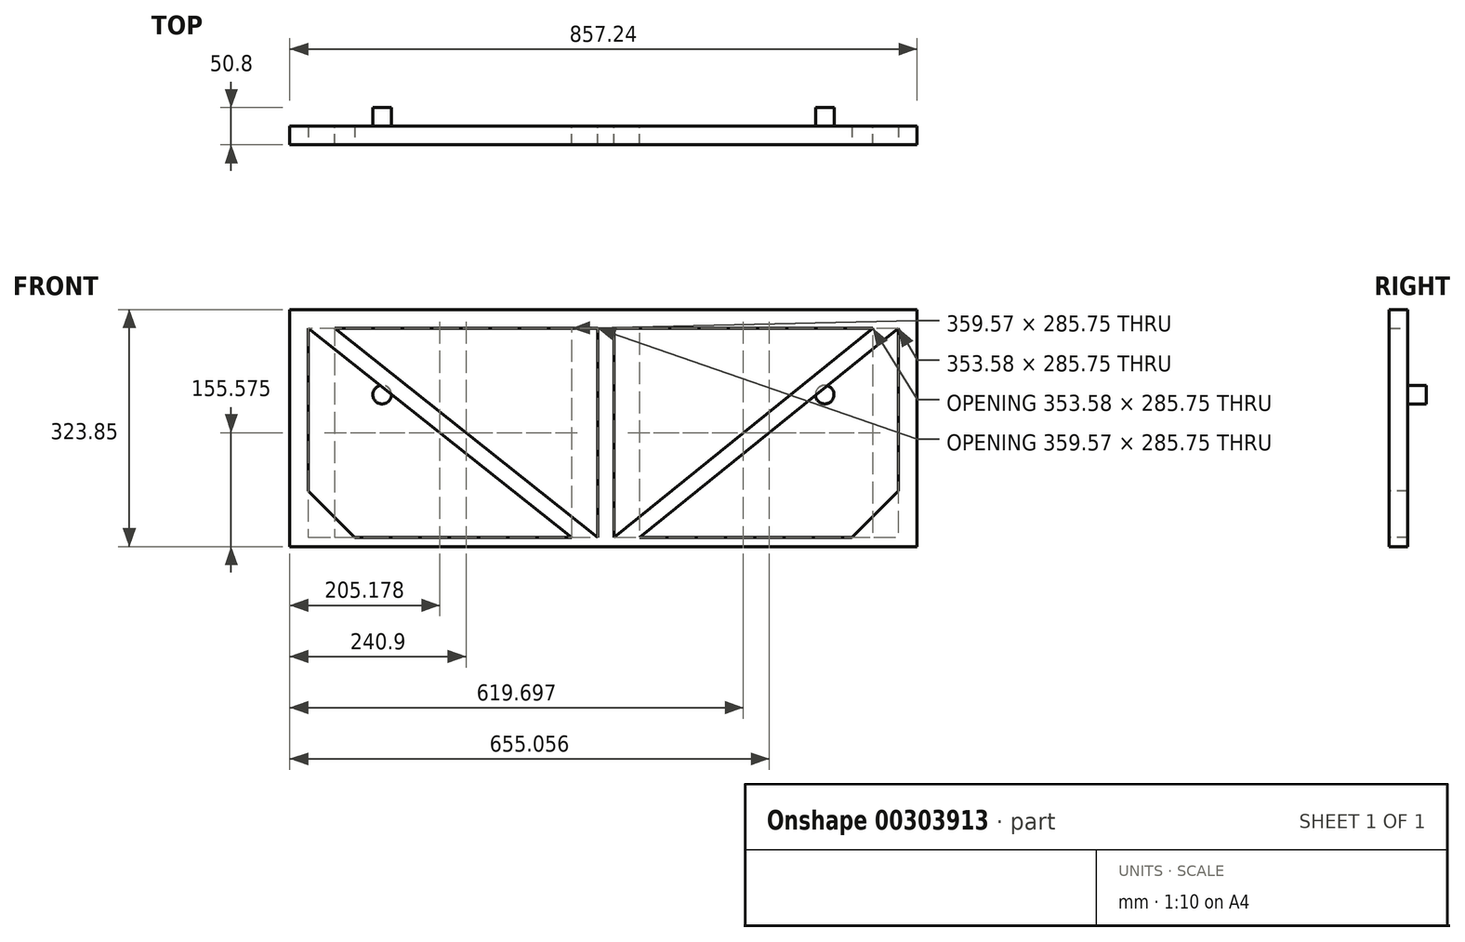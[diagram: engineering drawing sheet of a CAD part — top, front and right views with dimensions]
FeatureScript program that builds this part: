
annotation { "Feature Type Name" : "Feature", "Feature Type Description" : "" }
export const myFeature = defineFeature(function(context is Context, id is Id, definition is map)
    precondition{}
    {
        {
            var Q0;
            Q0=qCreatedBy(makeId("Front.planeOp"),FACE);
            var sketch = newSketch(context, id + "F0", { "sketchPlane" : qUnion([Q0])});
            skLineSegment(sketch, "E0.bottom", {"start": v(-428.63, 0) * mm, "end": v(428.63, 0) * mm, "construction": true});
            skLineSegment(sketch, "E0.left", {"start": v(-428.63, 0) * mm, "end": v(-428.63, 12.7) * mm, "construction": true});
            skLineSegment(sketch, "E0.right", {"start": v(428.63, 0) * mm, "end": v(428.63, 12.7) * mm, "construction": true});
            skLineSegment(sketch, "E1.left", {"start": v(428.63, 12.7) * mm, "end": v(428.63, 298.45) * mm});
            skLineSegment(sketch, "E1.right", {"start": v(403.23, 12.7) * mm, "end": v(403.23, 298.45) * mm});
            skLineSegment(sketch, "E2", {"start": v(-7.94, 12.7) * mm, "end": v(-7.94, 298.45) * mm});
            skLineSegment(sketch, "E3", {"start": v(14.29, 298.45) * mm, "end": v(14.29, 12.7) * mm});
            skLineSegment(sketch, "E4.top", {"start": v(-428.62, 323.85) * mm, "end": v(428.62, 323.85) * mm});
            skLineSegment(sketch, "E4.left", {"start": v(-428.62, 298.45) * mm, "end": v(-428.62, 323.85) * mm});
            skLineSegment(sketch, "E4.right", {"start": v(428.63, 298.45) * mm, "end": v(428.63, 323.85) * mm});
            skLineSegment(sketch, "E5.left", {"start": v(-428.63, 298.45) * mm, "end": v(-428.63, 12.7) * mm});
            skLineSegment(sketch, "E5.right", {"start": v(-403.23, 298.45) * mm, "end": v(-403.23, 12.7) * mm});
            skLineSegment(sketch, "E6", {"start": v(-403.23, 298.45) * mm, "end": v(-43.66, 12.7) * mm});
            skLineSegment(sketch, "E7", {"start": v(-7.94, 12.7) * mm, "end": v(-367.5, 298.45) * mm});
            skLineSegment(sketch, "E8", {"start": v(14.29, 12.7) * mm, "end": v(367.87, 298.45) * mm});
            skLineSegment(sketch, "E9", {"start": v(403.23, 298.45) * mm, "end": v(49.65, 12.7) * mm});
            skLineSegment(sketch, "E10.trimOffspring", {"start": v(-367.5, 298.45) * mm, "end": v(-7.94, 298.45) * mm});
            skLineSegment(sketch, "E11.trimOffspring", {"start": v(14.29, 298.45) * mm, "end": v(367.87, 298.45) * mm});
            skLineSegment(sketch, "E12.trimOffspring", {"start": v(403.23, 12.7) * mm, "end": v(428.63, 12.7) * mm});
            skLineSegment(sketch, "E13", {"start": v(-428.63, 12.7) * mm, "end": v(-403.23, 12.7) * mm});
            skLineSegment(sketch, "E14.trimOffspring", {"start": v(-43.66, 12.7) * mm, "end": v(49.65, 12.7) * mm});
            skLineSegment(sketch, "E15.bottom", {"start": v(-428.63, 12.7) * mm, "end": v(428.63, 12.7) * mm});
            skLineSegment(sketch, "E15.top", {"start": v(-428.63, 0) * mm, "end": v(428.63, 0) * mm});
            skLineSegment(sketch, "E15.left", {"start": v(-428.63, 12.7) * mm, "end": v(-428.63, 0) * mm});
            skLineSegment(sketch, "E15.right", {"start": v(428.63, 12.7) * mm, "end": v(428.63, 0) * mm});
            skLineSegment(sketch, "E16", {"start": v(-7.94, 106.7) * mm, "end": v(14.29, 106.7) * mm, "construction": true});
            skPoint(sketch, "E17", {"position": v(3.17, 106.7) * mm});
            skSolve(sketch);
        }
        {
            var Q0;
            Q0 = qSketchRegion(id + "F0", true);
            extrude(context, id + "F1", {"entities" : qUnion([Q0]), "depth" : 25.4 * mm});
        }
        {
            var Q0;
            Q0=makeQuery(id+"F1.opExtrude","CAP_FACE",FACE,{"disambiguationData":[OSD([sQuery(id+"F0.wireOp",EDGE,"E1.left"),sQuery(id+"F0.wireOp",EDGE,"E1.right"),sQuery(id+"F0.wireOp",EDGE,"E2"),sQuery(id+"F0.wireOp",EDGE,"E3"),sQuery(id+"F0.wireOp",EDGE,"E4.top"),sQuery(id+"F0.wireOp",EDGE,"E4.left"),sQuery(id+"F0.wireOp",EDGE,"E4.right"),sQuery(id+"F0.wireOp",EDGE,"E5.left"),sQuery(id+"F0.wireOp",EDGE,"E5.right"),sQuery(id+"F0.wireOp",EDGE,"E6"),sQuery(id+"F0.wireOp",EDGE,"E7"),sQuery(id+"F0.wireOp",EDGE,"E8"),sQuery(id+"F0.wireOp",EDGE,"E9"),sQuery(id+"F0.wireOp",EDGE,"E10.trimOffspring"),sQuery(id+"F0.wireOp",EDGE,"E11.trimOffspring"),sQuery(id+"F0.wireOp",EDGE,"E15.bottom"),sQuery(id+"F0.wireOp",EDGE,"E15.top"),sQuery(id+"F0.wireOp",EDGE,"E15.left"),sQuery(id+"F0.wireOp",EDGE,"E15.right")])],"isStart":false});
            var sketch = newSketch(context, id + "F2", { "sketchPlane" : qUnion([Q0])});
            skLineSegment(sketch, "E18", {"start": v(-403.23, 76.2) * mm, "end": v(-339.73, 12.7) * mm});
            skLineSegment(sketch, "E19", {"start": v(339.73, 12.7) * mm, "end": v(403.23, 76.2) * mm});
            skLineSegment(sketch, "E20", {"start": v(-403.23, 76.2) * mm, "end": v(-403.23, 12.7) * mm});
            skLineSegment(sketch, "E21", {"start": v(-403.23, 12.7) * mm, "end": v(-339.73, 12.7) * mm});
            skLineSegment(sketch, "E22", {"start": v(339.73, 12.7) * mm, "end": v(403.23, 12.7) * mm});
            skLineSegment(sketch, "E23", {"start": v(403.23, 12.7) * mm, "end": v(403.23, 76.2) * mm});
            skSolve(sketch);
        }
        {
            var Q0;
            Q0 = qSketchRegion(id + "F2", true);
            var Q1;
            Q1=makeQuery(id+"F1.opExtrude","SWEPT_BODY",BODY,{"disambiguationData":[OSD([sQuery(id+"F0.wireOp",EDGE,"E1.left"),sQuery(id+"F0.wireOp",EDGE,"E1.right"),sQuery(id+"F0.wireOp",EDGE,"E2"),sQuery(id+"F0.wireOp",EDGE,"E3"),sQuery(id+"F0.wireOp",EDGE,"E4.top"),sQuery(id+"F0.wireOp",EDGE,"E4.left"),sQuery(id+"F0.wireOp",EDGE,"E4.right"),sQuery(id+"F0.wireOp",EDGE,"E5.left"),sQuery(id+"F0.wireOp",EDGE,"E5.right"),sQuery(id+"F0.wireOp",EDGE,"E6"),sQuery(id+"F0.wireOp",EDGE,"E7"),sQuery(id+"F0.wireOp",EDGE,"E8"),sQuery(id+"F0.wireOp",EDGE,"E9"),sQuery(id+"F0.wireOp",EDGE,"E10.trimOffspring"),sQuery(id+"F0.wireOp",EDGE,"E11.trimOffspring"),sQuery(id+"F0.wireOp",EDGE,"E15.bottom"),sQuery(id+"F0.wireOp",EDGE,"E15.top"),sQuery(id+"F0.wireOp",EDGE,"E15.left"),sQuery(id+"F0.wireOp",EDGE,"E15.right")])]});
            extrude(context, id + "F3", {"entities" : qUnion([Q0]), "operationType" : NewBodyOperationType.ADD, "oppositeDirection" : true, "endBoundEntityBody" : qUnion([Q1]), "depth" : 25.4 * mm});
        }
        {
            var Q0;
            Q0=qCreatedBy(makeId("Front.planeOp"),FACE);
            var sketch = newSketch(context, id + "F4", { "sketchPlane" : qUnion([Q0])});
            skCircle(sketch, "E24", {"center": v(302.4, 207.65) * mm, "radius": 12.7 * mm});
            skCircle(sketch, "E25", {"center": v(-302.4, 207.65) * mm, "radius": 12.7 * mm});
            skLineSegment(sketch, "E26.0", {"start": v(-428.62, 323.85) * mm, "end": v(428.63, 323.85) * mm, "construction": true});
            skLineSegment(sketch, "E27", {"start": v(0, 323.85) * mm, "end": v(0, 305.7) * mm, "construction": true});
            skPoint(sketch, "E27.endSnap0", {"position": v(0, 323.85) * mm});
            skSolve(sketch);
        }
        {
            var Q0;
            Q0=makeQuery(id+"F4.imprint","IMPRINT",FACE,{"disambiguationData":[TD([[makeQuery(id+"F4.imprint","IMPRINT",EDGE,{"derivedFrom":sQuery(id+"F4.wireOp",EDGE,"E25")}),1.0]])]});
            var Q1;
            Q1=makeQuery(id+"F4.imprint","IMPRINT",FACE,{"disambiguationData":[TD([[makeQuery(id+"F4.imprint","IMPRINT",EDGE,{"derivedFrom":sQuery(id+"F4.wireOp",EDGE,"E24")}),1.0]])]});
            var Q2;
            Q2=sQuery(id+"F4.wireOp",EDGE,"E24");
            var Q3;
            Q3=sQuery(id+"F4.wireOp",EDGE,"E25");
            var Q4;
            Q4=makeQuery(id+"F3.boolean.opBoolean","MERGE",FACE,{"derivedFrom":[makeQuery(id+"F1.opExtrude","CAP_FACE",FACE,{"disambiguationData":[OSD([sQuery(id+"F0.wireOp",EDGE,"E1.left"),sQuery(id+"F0.wireOp",EDGE,"E1.right"),sQuery(id+"F0.wireOp",EDGE,"E2"),sQuery(id+"F0.wireOp",EDGE,"E3"),sQuery(id+"F0.wireOp",EDGE,"E4.top"),sQuery(id+"F0.wireOp",EDGE,"E4.left"),sQuery(id+"F0.wireOp",EDGE,"E4.right"),sQuery(id+"F0.wireOp",EDGE,"E5.left"),sQuery(id+"F0.wireOp",EDGE,"E5.right"),sQuery(id+"F0.wireOp",EDGE,"E6"),sQuery(id+"F0.wireOp",EDGE,"E7"),sQuery(id+"F0.wireOp",EDGE,"E8"),sQuery(id+"F0.wireOp",EDGE,"E9"),sQuery(id+"F0.wireOp",EDGE,"E10.trimOffspring"),sQuery(id+"F0.wireOp",EDGE,"E11.trimOffspring"),sQuery(id+"F0.wireOp",EDGE,"E15.bottom"),sQuery(id+"F0.wireOp",EDGE,"E15.top"),sQuery(id+"F0.wireOp",EDGE,"E15.left"),sQuery(id+"F0.wireOp",EDGE,"E15.right")])],"isStart":false}),makeQuery(id+"F3.opExtrude","CAP_FACE",FACE,{"disambiguationData":[OSD([sQuery(id+"F2.wireOp",EDGE,"E18"),sQuery(id+"F2.wireOp",EDGE,"E20"),sQuery(id+"F2.wireOp",EDGE,"E21")])],"isStart":true}),makeQuery(id+"F3.opExtrude","CAP_FACE",FACE,{"disambiguationData":[OSD([sQuery(id+"F2.wireOp",EDGE,"E19"),sQuery(id+"F2.wireOp",EDGE,"E22"),sQuery(id+"F2.wireOp",EDGE,"E23")])],"isStart":true})]});
            var Q5;
            Q5=makeQuery(id+"F1.opExtrude","SWEPT_BODY",BODY,{"disambiguationData":[OSD([sQuery(id+"F0.wireOp",EDGE,"E1.left"),sQuery(id+"F0.wireOp",EDGE,"E1.right"),sQuery(id+"F0.wireOp",EDGE,"E2"),sQuery(id+"F0.wireOp",EDGE,"E3"),sQuery(id+"F0.wireOp",EDGE,"E4.top"),sQuery(id+"F0.wireOp",EDGE,"E4.left"),sQuery(id+"F0.wireOp",EDGE,"E4.right"),sQuery(id+"F0.wireOp",EDGE,"E5.left"),sQuery(id+"F0.wireOp",EDGE,"E5.right"),sQuery(id+"F0.wireOp",EDGE,"E6"),sQuery(id+"F0.wireOp",EDGE,"E7"),sQuery(id+"F0.wireOp",EDGE,"E8"),sQuery(id+"F0.wireOp",EDGE,"E9"),sQuery(id+"F0.wireOp",EDGE,"E10.trimOffspring"),sQuery(id+"F0.wireOp",EDGE,"E11.trimOffspring"),sQuery(id+"F0.wireOp",EDGE,"E15.bottom"),sQuery(id+"F0.wireOp",EDGE,"E15.top"),sQuery(id+"F0.wireOp",EDGE,"E15.left"),sQuery(id+"F0.wireOp",EDGE,"E15.right")])]});
            extrude(context, id + "F5", {"entities" : qUnion([Q0, Q1]), "operationType" : NewBodyOperationType.ADD, "surfaceEntities" : qUnion([Q2, Q3]), "oppositeDirection" : true, "depth" : 25.4 * mm});
        }
    });
